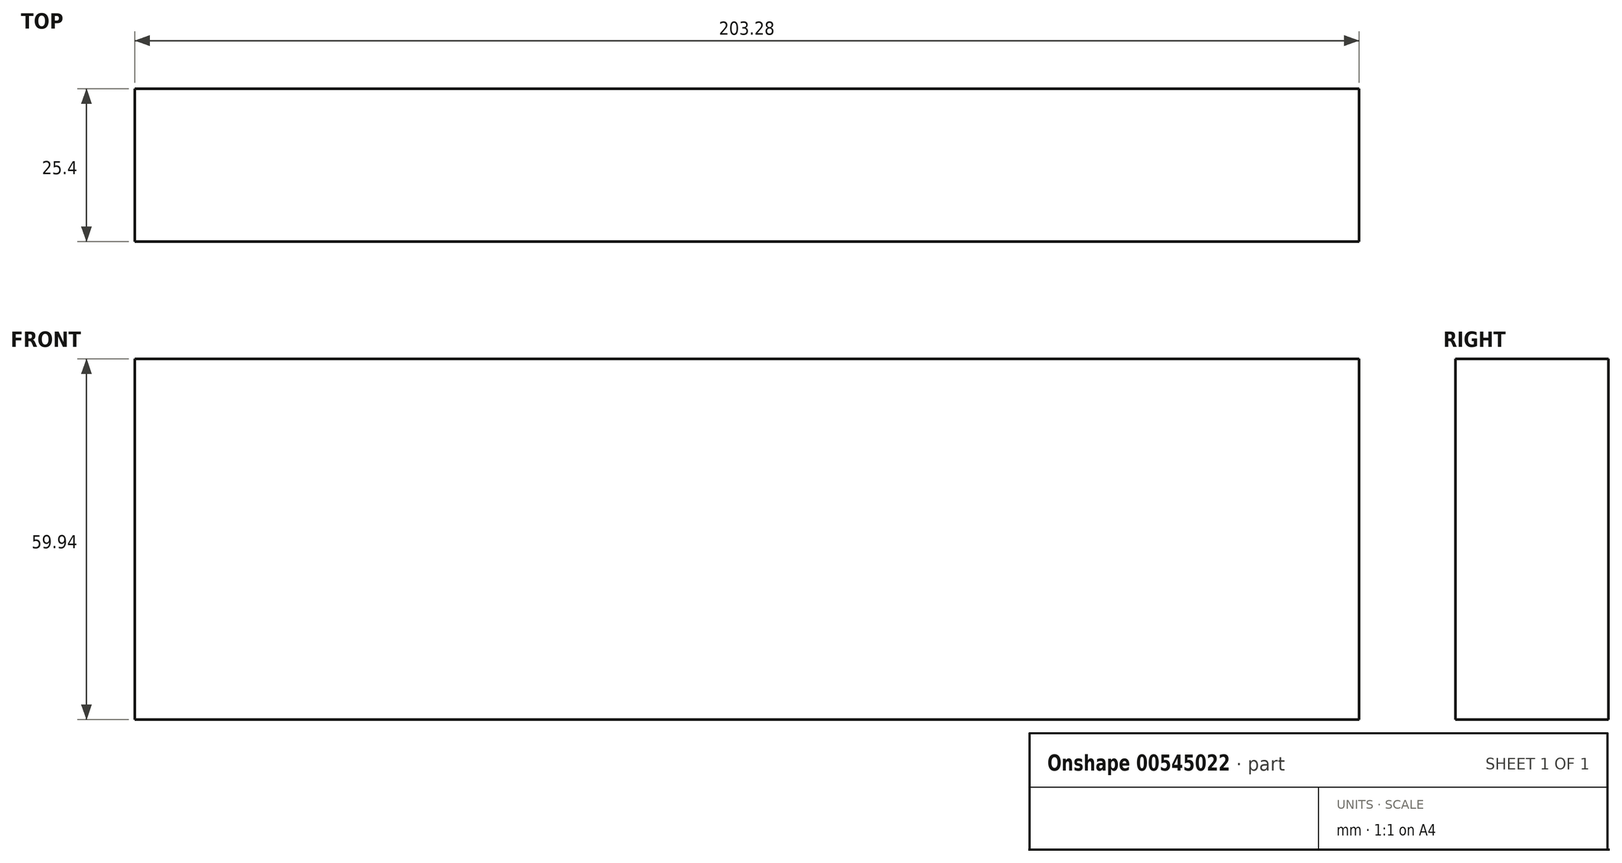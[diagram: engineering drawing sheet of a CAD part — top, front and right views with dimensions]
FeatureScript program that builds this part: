
annotation { "Feature Type Name" : "Feature", "Feature Type Description" : "" }
export const myFeature = defineFeature(function(context is Context, id is Id, definition is map)
    precondition{}
    {
        {
            var Q0;
            Q0=qCreatedBy(makeId("Front.planeOp"),FACE);
            var sketch = newSketch(context, id + "F0", { "sketchPlane" : qUnion([Q0])});
            skLineSegment(sketch, "E0.bottom", {"start": v(101.64, -29.97) * mm, "end": v(-101.64, -29.97) * mm});
            skLineSegment(sketch, "E0.top", {"start": v(101.64, 29.97) * mm, "end": v(-101.64, 29.97) * mm});
            skLineSegment(sketch, "E0.left", {"start": v(101.64, -29.97) * mm, "end": v(101.64, 29.97) * mm});
            skLineSegment(sketch, "E0.right", {"start": v(-101.64, -29.97) * mm, "end": v(-101.64, 29.97) * mm});
            skPoint(sketch, "E0.middle", {"position": v(0, 0) * mm});
            skSolve(sketch);
        }
        {
            var Q0;
            Q0 = qSketchRegion(id + "F0", true);
            var Q1;
            Q1=makeQuery(id+"F0.imprint","IMPRINT",FACE,{"disambiguationData":[TD([[makeQuery(id+"F0.imprint","IMPRINT",EDGE,{"derivedFrom":sQuery(id+"F0.wireOp",EDGE,"E0.bottom")}),-1.0]])]});
            extrude(context, id + "F1", {"entities" : qUnion([Q0, Q1]), "depth" : 25.4 * mm, "offsetDistance" : 25.4 * mm});
        }
    });
